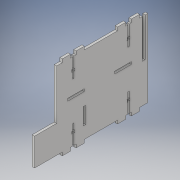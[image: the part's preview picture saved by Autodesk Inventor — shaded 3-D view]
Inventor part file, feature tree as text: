
AUTODESK INVENTOR PART (.ipt)
format: ipt  version: 2018 (Build 220112000, 112)  size: 224,256 bytes
history: native  units: in
note: dims shown in document units (in); Inventor stores cm internally (conversion verified against a paired STEP export)
features: extrude x4, sketch x4
ambient origin geometry x8: Origin, YZ Plane, XZ Plane, XY Plane, X Axis, Y Axis, Z Axis, Center Point
bodies: Solid1 (feature_tree)
feature tree (8):
  extrude  "Extrusion1"  Depth=10.25in
  extrude  "Extrusion2"  Depth=1.5in
  extrude  "Extrusion3"  Depth=0.25in
  extrude  "Extrusion4"  Depth=1.0in TaperAngle=0.0deg
  sketch  "Sketch1"  dims[d0=7.0in d1=10.25in]
  sketch  "Sketch2"  dims[d8=1.5in d16=0.01in]
  sketch  "Sketch3"  dims[d17=0.01in d18=0.25in]
  sketch  "Sketch4"  dims[d19=0.2188in d20=0.0in d21=1.0in d22=0.0in d28=1.0in d29=0.0in d33=1.0in d34=0.0in]
